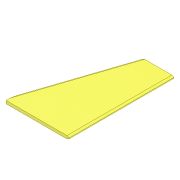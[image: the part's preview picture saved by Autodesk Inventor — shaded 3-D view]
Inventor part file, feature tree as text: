
AUTODESK INVENTOR PART (.ipt)
format: ipt  version: 2022 (Build 260153000, 153)  size: 125,440 bytes
history: native  units: mm
features: chamfer x4, extrude x3, sketch x3, plane x1, projected_geometry x1
ambient origin geometry x8: Origin, YZ Plane, XZ Plane, XY Plane, X Axis, Y Axis, Z Axis, Center Point
bodies: Solid1 (feature_tree)
feature tree (12):
  extrude  "Extrusion1"  Depth=600.0mm
  extrude  "Extrusion2"  Depth=28.0mm TaperAngle=0.0deg
  plane  "Work Plane1"
  extrude  "Extrusion3"  Depth=100.0mm
  chamfer  "Chamfer1"  Distance=16.0mm
  chamfer  "Chamfer2"  Distance=305.0mm
  chamfer  "Chamfer3"  Distance=20.0mm
  chamfer  "Chamfer4"  Distance=16.0mm
  sketch  "Sketch1"  dims[d0=1000.0mm d1=600.0mm]
  sketch  "Sketch2"  dims[d2=28.0mm d3=0.0mm d5=200.0mm d6=0.0mm]
  projected_geometry  "Projected Loop1"
  sketch  "Sketch3"  dims[d7=300.0mm d8=100.0mm d9=16.0mm d10=305.0mm d11=20.0mm d12=16.0mm d13=395.0mm d14=20.0mm d15=16.0mm d16=350.0mm d17=75.0mm d18=16.0mm d19=350.0mm d20=160.0mm d21=200.0mm d22=0.0mm d23=20.0mm d24=10.0mm d25=45.0deg d26=10.0mm d27=20.0mm d28=45.0deg d29=20.0mm d30=10.0mm d31=45.0deg d32=20.0mm d33=10.0mm d34=45.0deg]
